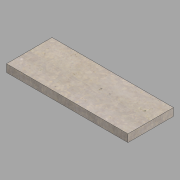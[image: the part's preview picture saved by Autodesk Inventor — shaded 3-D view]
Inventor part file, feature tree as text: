
AUTODESK INVENTOR PART (.ipt)
format: ipt  version: 2022 (Build 260153000, 153)  size: 112,640 bytes
history: native  units: in
note: dims shown in document units (in); Inventor stores cm internally (conversion verified against a paired STEP export)
features: extrude x1, sketch x1
ambient origin geometry x8: Origin, YZ Plane, XZ Plane, XY Plane, X Axis, Y Axis, Z Axis, Center Point
bodies: Solid1 (feature_tree)
feature tree (2):
  extrude  "Extrusion1"  Depth=18.0in
  sketch  "Sketch1"  dims[d0=48.0in d1=18.0in d2=3.0in d3=0.0in]
